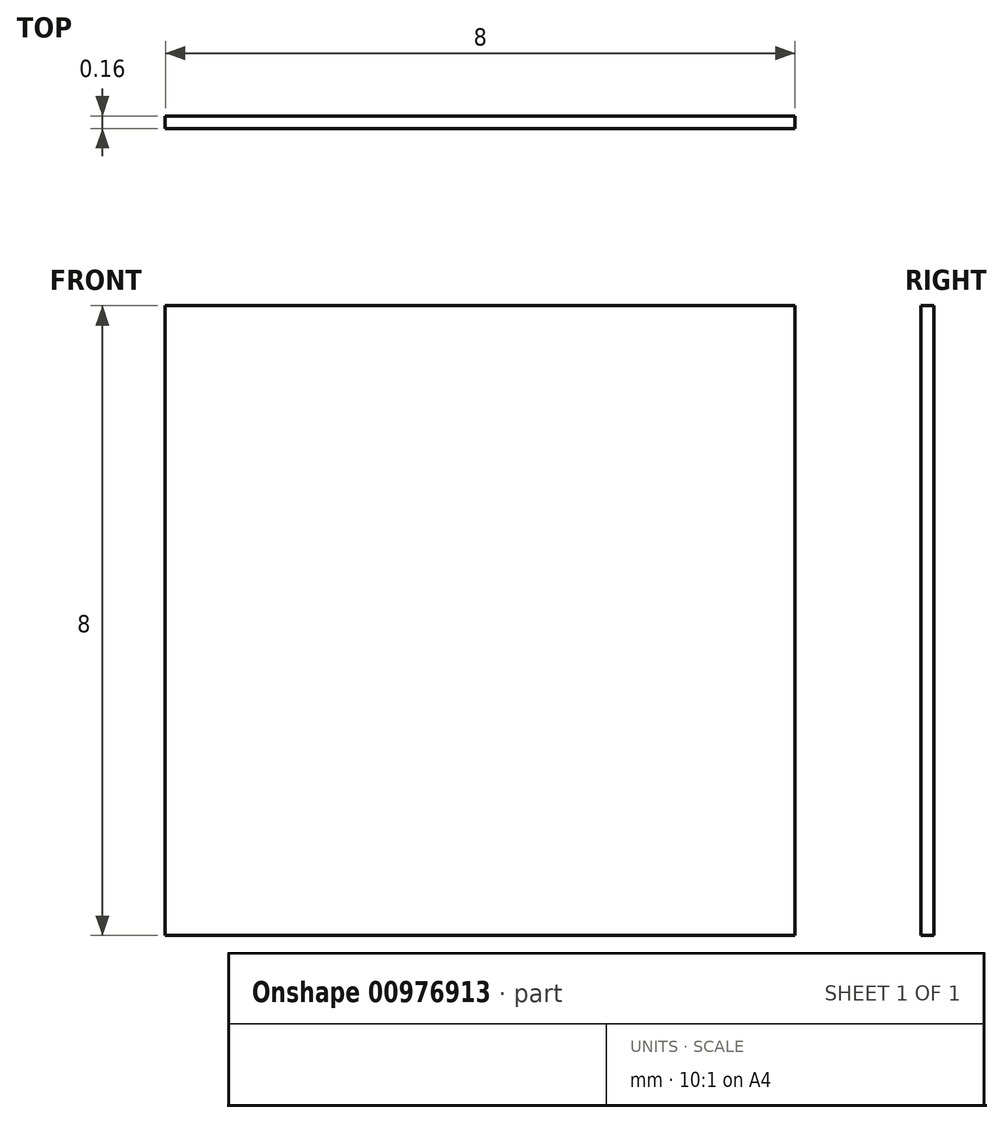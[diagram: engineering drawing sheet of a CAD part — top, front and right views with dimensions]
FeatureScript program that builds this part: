
annotation { "Feature Type Name" : "Feature", "Feature Type Description" : "" }
export const myFeature = defineFeature(function(context is Context, id is Id, definition is map)
    precondition{}
    {
        {
            assignVariable(context, id + "F0", {"name" : "hei", "anyValue" : .16});
        }
        {
            var Q0;
            Q0=qCreatedBy(makeId("Front.planeOp"),FACE);
            var sketch = newSketch(context, id + "F1", { "sketchPlane" : qUnion([Q0])});
            skLineSegment(sketch, "E0.bottom", {"start": v(4, 4) * mm, "end": v(-4, 4) * mm});
            skLineSegment(sketch, "E0.top", {"start": v(4, -4) * mm, "end": v(-4, -4) * mm});
            skLineSegment(sketch, "E0.left", {"start": v(4, 4) * mm, "end": v(4, -4) * mm});
            skLineSegment(sketch, "E0.right", {"start": v(-4, 4) * mm, "end": v(-4, -4) * mm});
            skPoint(sketch, "E0.middle", {"position": v(0, 0) * mm});
            skSolve(sketch);
        }
        {
            var Q0;
            Q0=makeQuery(id+"F1.imprint","IMPRINT",FACE,{"disambiguationData":[TD([[makeQuery(id+"F1.imprint","IMPRINT",EDGE,{"derivedFrom":sQuery(id+"F1.wireOp",EDGE,"E0.bottom")}),1.0]])]});
            extrude(context, id + "F2", {"entities" : qUnion([Q0]), "depth" : (getVariable(context, 'hei')) * mm, "offsetDistance" : 25.4 * mm});
        }
    });
